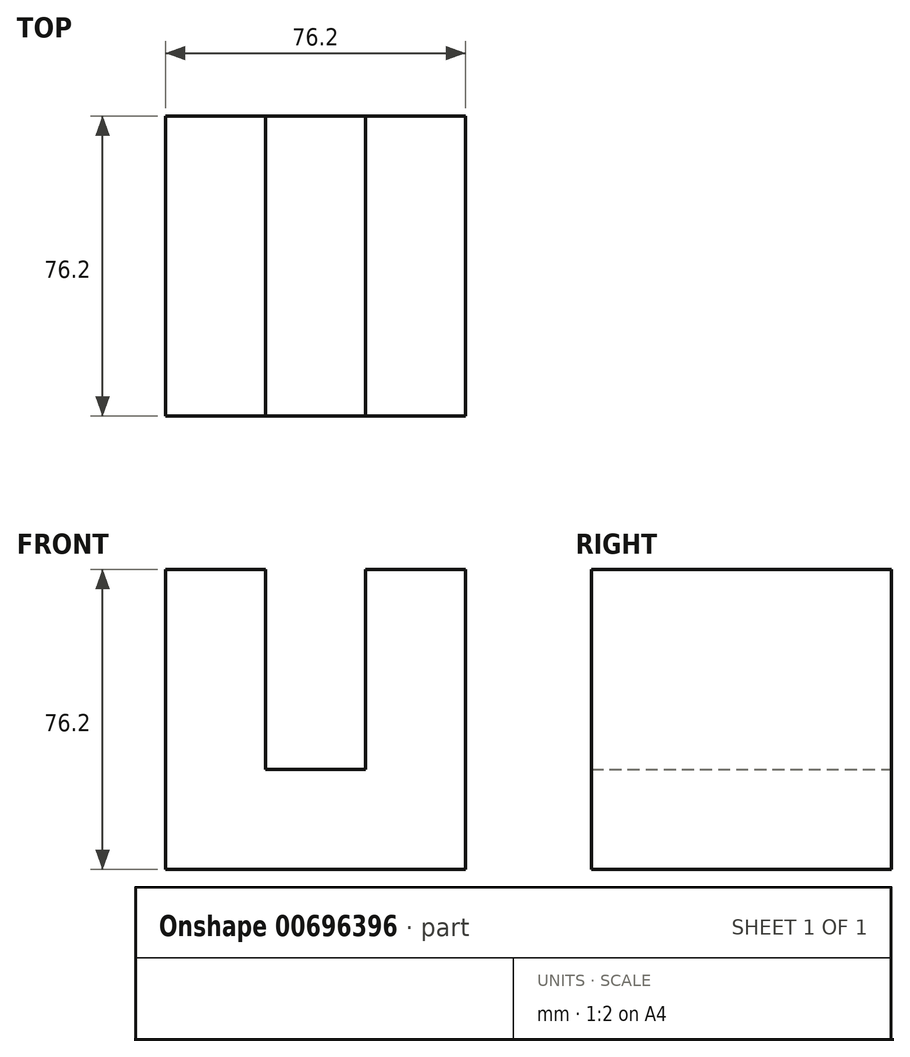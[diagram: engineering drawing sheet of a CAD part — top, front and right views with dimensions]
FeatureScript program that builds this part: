
annotation { "Feature Type Name" : "Feature", "Feature Type Description" : "" }
export const myFeature = defineFeature(function(context is Context, id is Id, definition is map)
    precondition{}
    {
        {
            var Q0;
            Q0=qCreatedBy(makeId("Front.planeOp"),FACE);
            var sketch = newSketch(context, id + "F0", { "sketchPlane" : qUnion([Q0])});
            skLineSegment(sketch, "E0", {"start": v(0, 0) * mm, "end": v(-76.2, 0) * mm});
            skLineSegment(sketch, "E1", {"start": v(-76.2, 0) * mm, "end": v(-76.2, 76.2) * mm});
            skLineSegment(sketch, "E2", {"start": v(0, 0) * mm, "end": v(0, 76.2) * mm});
            skLineSegment(sketch, "E3", {"start": v(0, 76.2) * mm, "end": v(-25.4, 76.2) * mm});
            skLineSegment(sketch, "E4", {"start": v(-76.2, 76.2) * mm, "end": v(-50.8, 76.2) * mm});
            skLineSegment(sketch, "E5", {"start": v(-50.8, 76.2) * mm, "end": v(-50.8, 25.4) * mm});
            skLineSegment(sketch, "E6", {"start": v(-25.4, 76.2) * mm, "end": v(-25.4, 25.4) * mm});
            skLineSegment(sketch, "E7", {"start": v(-25.4, 25.4) * mm, "end": v(-50.8, 25.4) * mm});
            skSolve(sketch);
        }
        {
            var Q0;
            Q0=makeQuery(id+"F0.imprint","IMPRINT",FACE,{"disambiguationData":[TD([[makeQuery(id+"F0.imprint","IMPRINT",EDGE,{"derivedFrom":sQuery(id+"F0.wireOp",EDGE,"E0")}),-1.0]])]});
            extrude(context, id + "F1", {"entities" : qUnion([Q0]), "depth" : 76.2 * mm, "offsetDistance" : 25.4 * mm});
        }
    });
